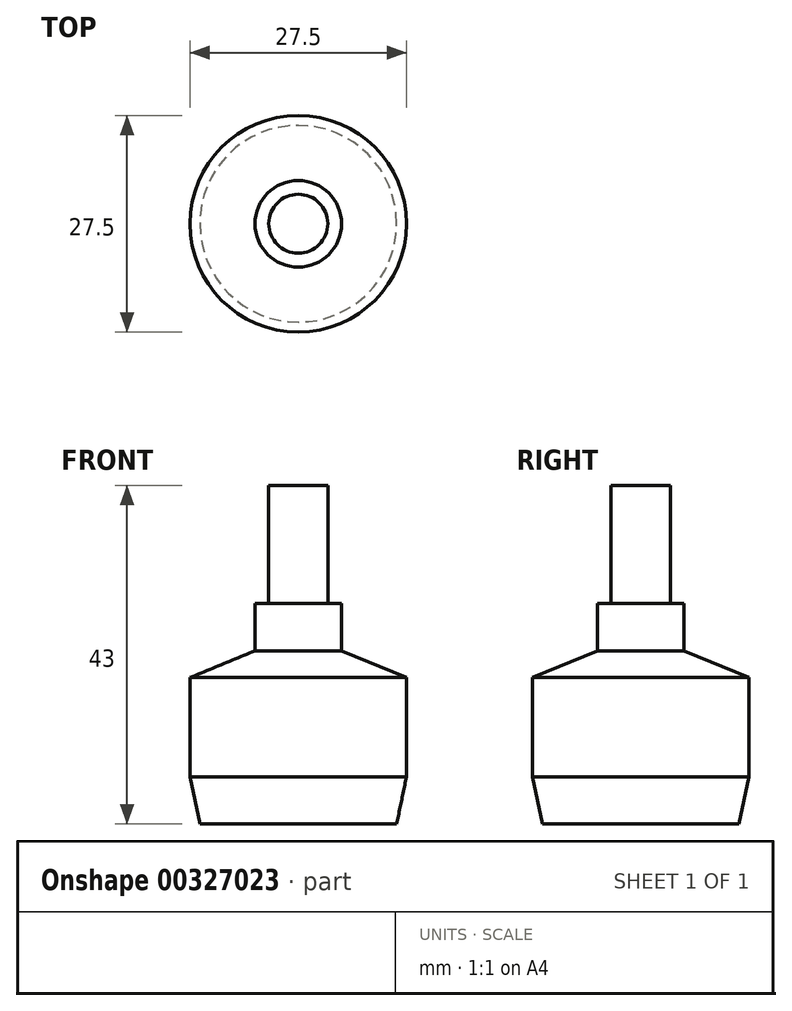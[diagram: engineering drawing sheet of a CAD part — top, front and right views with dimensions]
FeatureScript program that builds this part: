
annotation { "Feature Type Name" : "Feature", "Feature Type Description" : "" }
export const myFeature = defineFeature(function(context is Context, id is Id, definition is map)
    precondition{}
    {
        {
            var Q0;
            Q0=qCreatedBy(makeId("Top.planeOp"),FACE);
            var sketch = newSketch(context, id + "F0", { "sketchPlane" : qUnion([Q0])});
            skCircle(sketch, "E0", {"center": v(0, 0) * mm, "radius": 13.75 * mm});
            skCircle(sketch, "E1", {"center": v(0, 0) * mm, "radius": 5.5 * mm});
            skCircle(sketch, "E2", {"center": v(0, 0) * mm, "radius": 3.75 * mm});
            skCircle(sketch, "E3", {"center": v(0, 0) * mm, "radius": 12.5 * mm});
            skSolve(sketch);
        }
        {
            var Q0;
            Q0 = qSketchRegion(id + "F0", true);
            var Q1;
            Q1=makeQuery(id+"F0.imprint","IMPRINT",FACE,{"disambiguationData":[TD([[makeQuery(id+"F0.imprint","IMPRINT",EDGE,{"derivedFrom":sQuery(id+"F0.wireOp",EDGE,"E1")}),-1.0]])]});
            var Q2;
            Q2=makeQuery(id+"F0.imprint","IMPRINT",FACE,{"disambiguationData":[TD([[makeQuery(id+"F0.imprint","IMPRINT",EDGE,{"derivedFrom":sQuery(id+"F0.wireOp",EDGE,"E1")}),1.0]])]});
            var Q3;
            Q3=makeQuery(id+"F0.imprint","IMPRINT",FACE,{"disambiguationData":[TD([[makeQuery(id+"F0.imprint","IMPRINT",EDGE,{"derivedFrom":sQuery(id+"F0.wireOp",EDGE,"E2")}),1.0]])]});
            extrude(context, id + "F1", {"entities" : qUnion([Q0, Q1, Q2, Q3]), "depth" : 18.5 * mm, "hasSecondDirection" : true, "secondDirectionOppositeDirection" : false, "secondDirectionDepth" : 6 * mm});
        }
        {
            var Q0;
            Q0=makeQuery(id+"F0.imprint","IMPRINT",FACE,{"disambiguationData":[TD([[makeQuery(id+"F0.imprint","IMPRINT",EDGE,{"derivedFrom":sQuery(id+"F0.wireOp",EDGE,"E1")}),1.0]])]});
            var Q1;
            Q1=makeQuery(id+"F0.imprint","IMPRINT",FACE,{"disambiguationData":[TD([[makeQuery(id+"F0.imprint","IMPRINT",EDGE,{"derivedFrom":sQuery(id+"F0.wireOp",EDGE,"E2")}),1.0]])]});
            extrude(context, id + "F2", {"entities" : qUnion([Q0, Q1]), "operationType" : NewBodyOperationType.ADD, "depth" : 22 * mm});
        }
        {
            var Q0;
            Q0=makeQuery(id+"F0.imprint","IMPRINT",FACE,{"disambiguationData":[TD([[makeQuery(id+"F0.imprint","IMPRINT",EDGE,{"derivedFrom":sQuery(id+"F0.wireOp",EDGE,"E2")}),1.0]])]});
            var Q1;
            Q1=makeQuery(id+"F0.imprint","IMPRINT",FACE,{"disambiguationData":[TD([[makeQuery(id+"F0.imprint","IMPRINT",EDGE,{"derivedFrom":sQuery(id+"F0.wireOp",EDGE,"E1")}),1.0]])]});
            extrude(context, id + "F3", {"entities" : qUnion([Q0, Q1]), "operationType" : NewBodyOperationType.ADD, "depth" : 28 * mm});
        }
        {
            var Q0;
            Q0=makeQuery(id+"F0.imprint","IMPRINT",FACE,{"disambiguationData":[TD([[makeQuery(id+"F0.imprint","IMPRINT",EDGE,{"derivedFrom":sQuery(id+"F0.wireOp",EDGE,"E1")}),-1.0]])]});
            extrude(context, id + "F4", {"entities" : qUnion([Q0]), "operationType" : NewBodyOperationType.ADD, "depth" : 7 * mm});
        }
        {
            var Q0;
            Q0=makeQuery(id+"F4.boolean.opBoolean","INTERSECT",EDGE,{"derivedFrom":[makeQuery(id+"F1.opExtrude","CAP_FACE",FACE,{"disambiguationData":[OSD([sQuery(id+"F0.wireOp",EDGE,"E0")])],"isStart":true}),makeQuery(id+"F4.opExtrude","SWEPT_FACE",FACE,{"disambiguationData":[OSD([sQuery(id+"F0.wireOp",EDGE,"E3")])]})]});
            chamfer(context, id + "F5", {"entities" : qUnion([Q0]), "chamferType" : ChamferType.TWO_OFFSETS, "width1" : 6 * mm, "oppositeDirection" : false, "width2" : 1.25 * mm, "tangentPropagation" : true});
        }
        {
            var Q0;
            Q0=makeQuery(id+"F2.boolean.opBoolean","INTERSECT",EDGE,{"derivedFrom":[makeQuery(id+"F1.opExtrude","CAP_FACE",FACE,{"disambiguationData":[OSD([sQuery(id+"F0.wireOp",EDGE,"E0")])],"isStart":false}),makeQuery(id+"F2.opExtrude","SWEPT_FACE",FACE,{"disambiguationData":[OSD([sQuery(id+"F0.wireOp",EDGE,"E1")])]})]});
            chamfer(context, id + "F6", {"entities" : qUnion([Q0]), "chamferType" : ChamferType.TWO_OFFSETS, "width1" : 8.5 * mm, "oppositeDirection" : false, "width2" : 3.5 * mm, "tangentPropagation" : true});
        }
        {
            var Q0;
            Q0=makeQuery(id+"F0.imprint","IMPRINT",FACE,{"disambiguationData":[TD([[makeQuery(id+"F0.imprint","IMPRINT",EDGE,{"derivedFrom":sQuery(id+"F0.wireOp",EDGE,"E2")}),1.0]])]});
            extrude(context, id + "F7", {"entities" : qUnion([Q0]), "operationType" : NewBodyOperationType.ADD, "depth" : 43 * mm});
        }
    });
